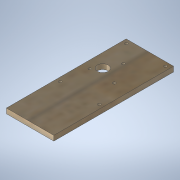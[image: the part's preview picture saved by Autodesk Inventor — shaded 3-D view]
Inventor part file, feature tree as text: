
AUTODESK INVENTOR PART (.ipt)
format: ipt  version: 2020.3 (Build 243373000, 373)  size: 190,976 bytes
history: native  units: mm
features: sketch x7, hole x5, extrude x2, other x1, fillet x1
ambient origin geometry x8: Origin, YZ Plane, XZ Plane, XY Plane, X Axis, Y Axis, Z Axis, Center Point
bodies: Body1 (feature_tree)
feature tree (16):
  other  "ソリッド1"
  extrude  "押し出し1"  Depth=81.509668mm
  hole  "穴1"  [1 undecoded]
  hole  "穴2"  [1 undecoded]
  hole  "穴3"  [1 undecoded]
  extrude  "押し出し2"  Depth=4.5mm
  hole  "穴4"  [1 undecoded]
  hole  "穴5"  [1 undecoded]
  fillet  "フィレット2"  Radius=4.5mm
  sketch  "スケッチ1"
  sketch  "スケッチ2"
  sketch  "スケッチ3"
  sketch  "スケッチ4"
  sketch  "スケッチ5"
  sketch  "スケッチ6"
  sketch  "スケッチ7"
note: 5 required parameter values undecoded (feature->parameter linkage not recoverable at this tier; creation-order binding heuristic only, values carry confidence <= 0.55)
